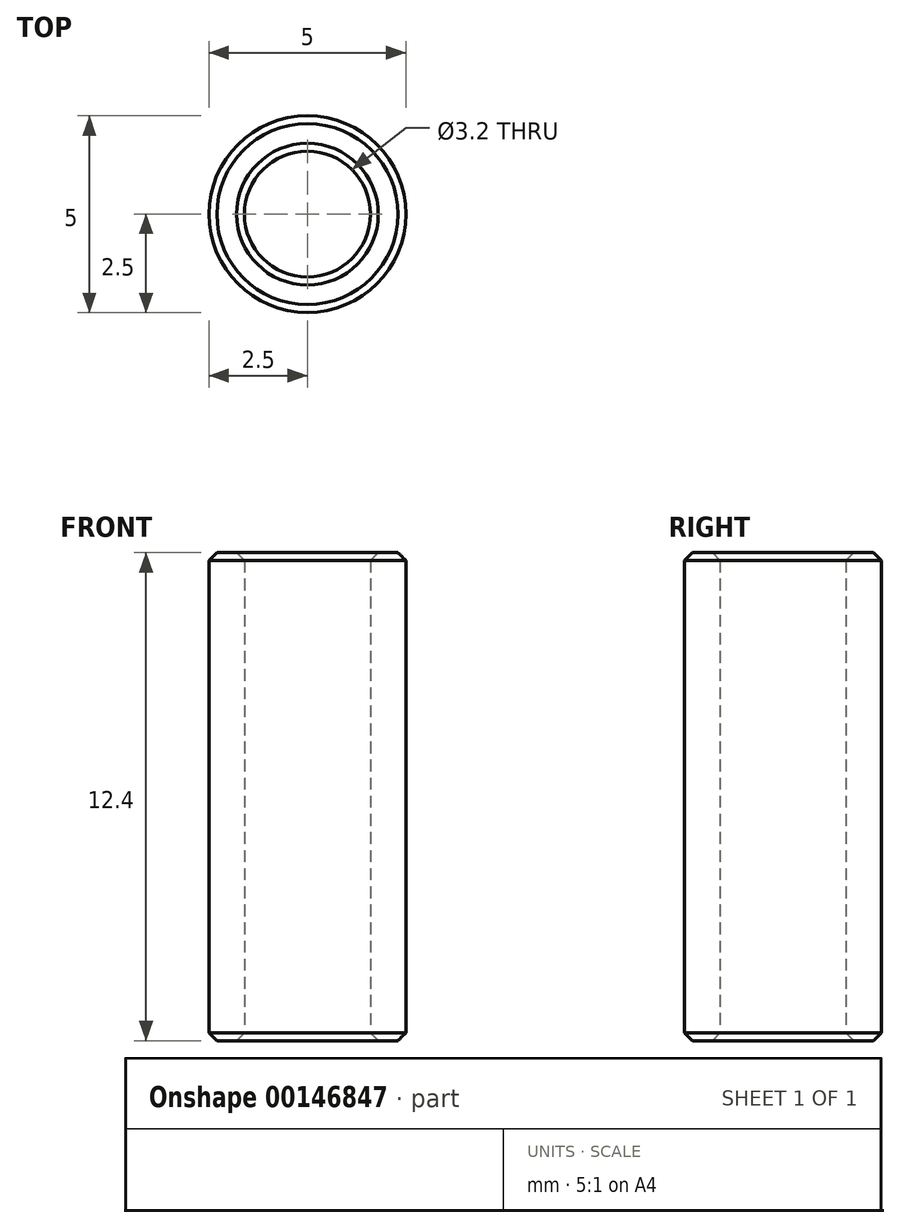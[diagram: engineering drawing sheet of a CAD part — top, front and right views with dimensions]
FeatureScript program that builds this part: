
annotation { "Feature Type Name" : "Feature", "Feature Type Description" : "" }
export const myFeature = defineFeature(function(context is Context, id is Id, definition is map)
    precondition{}
    {
        {
            var Q0;
            Q0=qCreatedBy(makeId("Top.planeOp"),FACE);
            var sketch = newSketch(context, id + "F0", { "sketchPlane" : qUnion([Q0])});
            skCircle(sketch, "E0", {"center": v(0, 0) * mm, "radius": 1.6 * mm});
            skCircle(sketch, "E1", {"center": v(0, 0) * mm, "radius": 2.5 * mm});
            skSolve(sketch);
        }
        {
            var Q0;
            Q0=qSketchRegion(id+"F0",true);
            extrude(context, id + "F1", {"entities" : qUnion([Q0]), "depth" : 12.4 * mm});
        }
        {
            var Q0;
            Q0=makeQuery(id+"F1.opExtrude","CAP_FACE",FACE,{"disambiguationData":[OSD([sQuery(id+"F0.wireOp",EDGE,"E0"),sQuery(id+"F0.wireOp",EDGE,"E1")])],"isStart":false});
            var Q1;
            Q1=makeQuery(id+"F1.opExtrude","CAP_EDGE",EDGE,{"disambiguationData":[OSD([sQuery(id+"F0.wireOp",EDGE,"E0")])],"isStart":true});
            var Q2;
            Q2=makeQuery(id+"F1.opExtrude","CAP_EDGE",EDGE,{"disambiguationData":[OSD([sQuery(id+"F0.wireOp",EDGE,"E1")])],"isStart":true});
            chamfer(context, id + "F2", {"entities" : qUnion([Q0, Q1, Q2]), "width" : 0.2 * mm, "tangentPropagation" : true});
        }
    });
